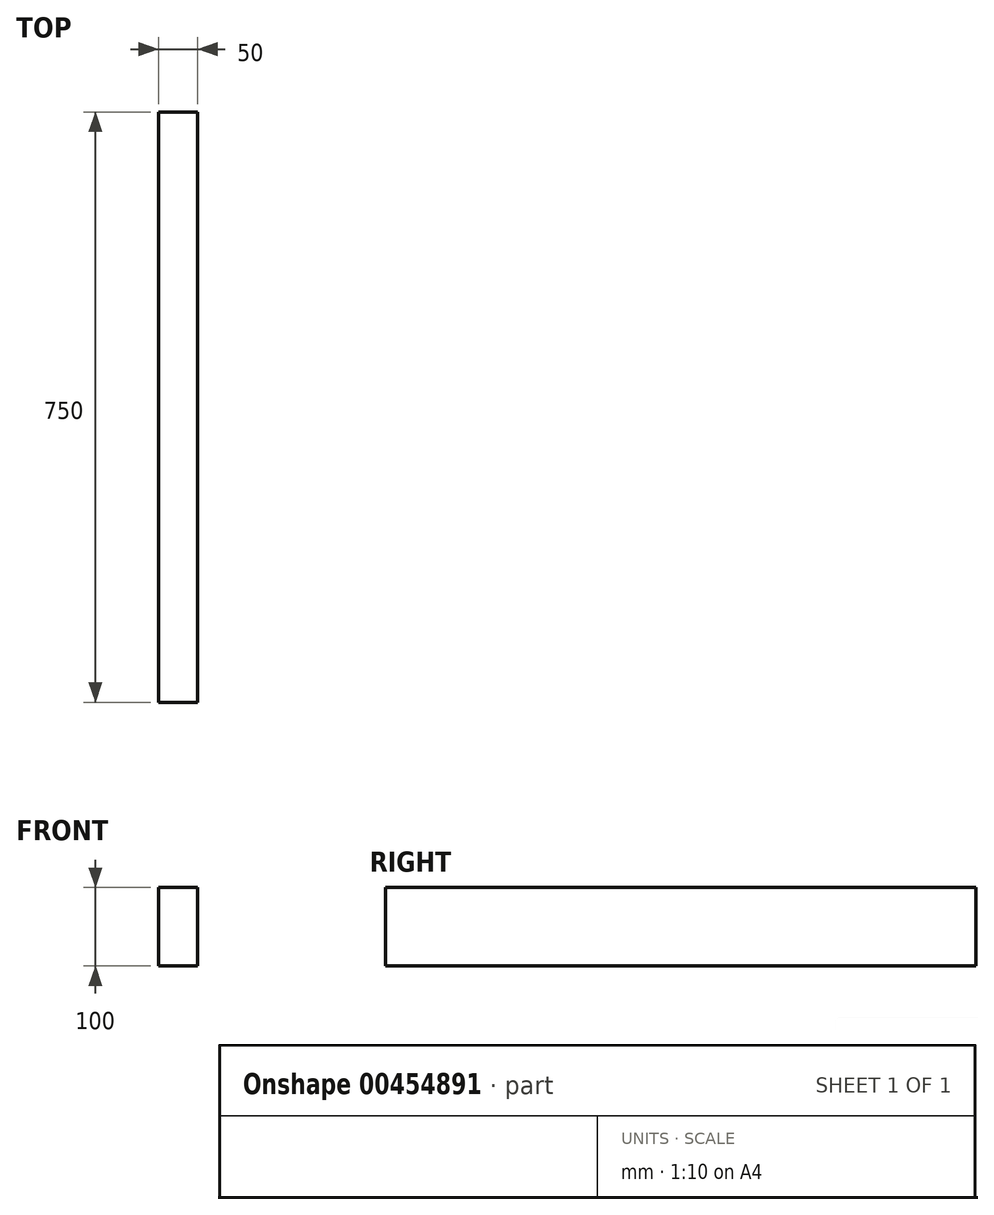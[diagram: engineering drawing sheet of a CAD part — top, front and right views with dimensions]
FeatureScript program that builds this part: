
annotation { "Feature Type Name" : "Feature", "Feature Type Description" : "" }
export const myFeature = defineFeature(function(context is Context, id is Id, definition is map)
    precondition{}
    {
        {
            var Q0;
            Q0=qCreatedBy(makeId("Front.planeOp"),FACE);
            var sketch = newSketch(context, id + "F0", { "sketchPlane" : qUnion([Q0])});
            skLineSegment(sketch, "E0.bottom", {"start": v(0, 0) * mm, "end": v(50, 0) * mm});
            skLineSegment(sketch, "E0.top", {"start": v(0, 100) * mm, "end": v(50, 100) * mm});
            skLineSegment(sketch, "E0.left", {"start": v(0, 0) * mm, "end": v(0, 100) * mm});
            skLineSegment(sketch, "E0.right", {"start": v(50, 0) * mm, "end": v(50, 100) * mm});
            skSolve(sketch);
        }
        {
            var Q0;
            Q0 = qSketchRegion(id + "F0", true);
            extrude(context, id + "F1", {"entities" : qUnion([Q0]), "depth" : 750 * mm});
        }
    });
